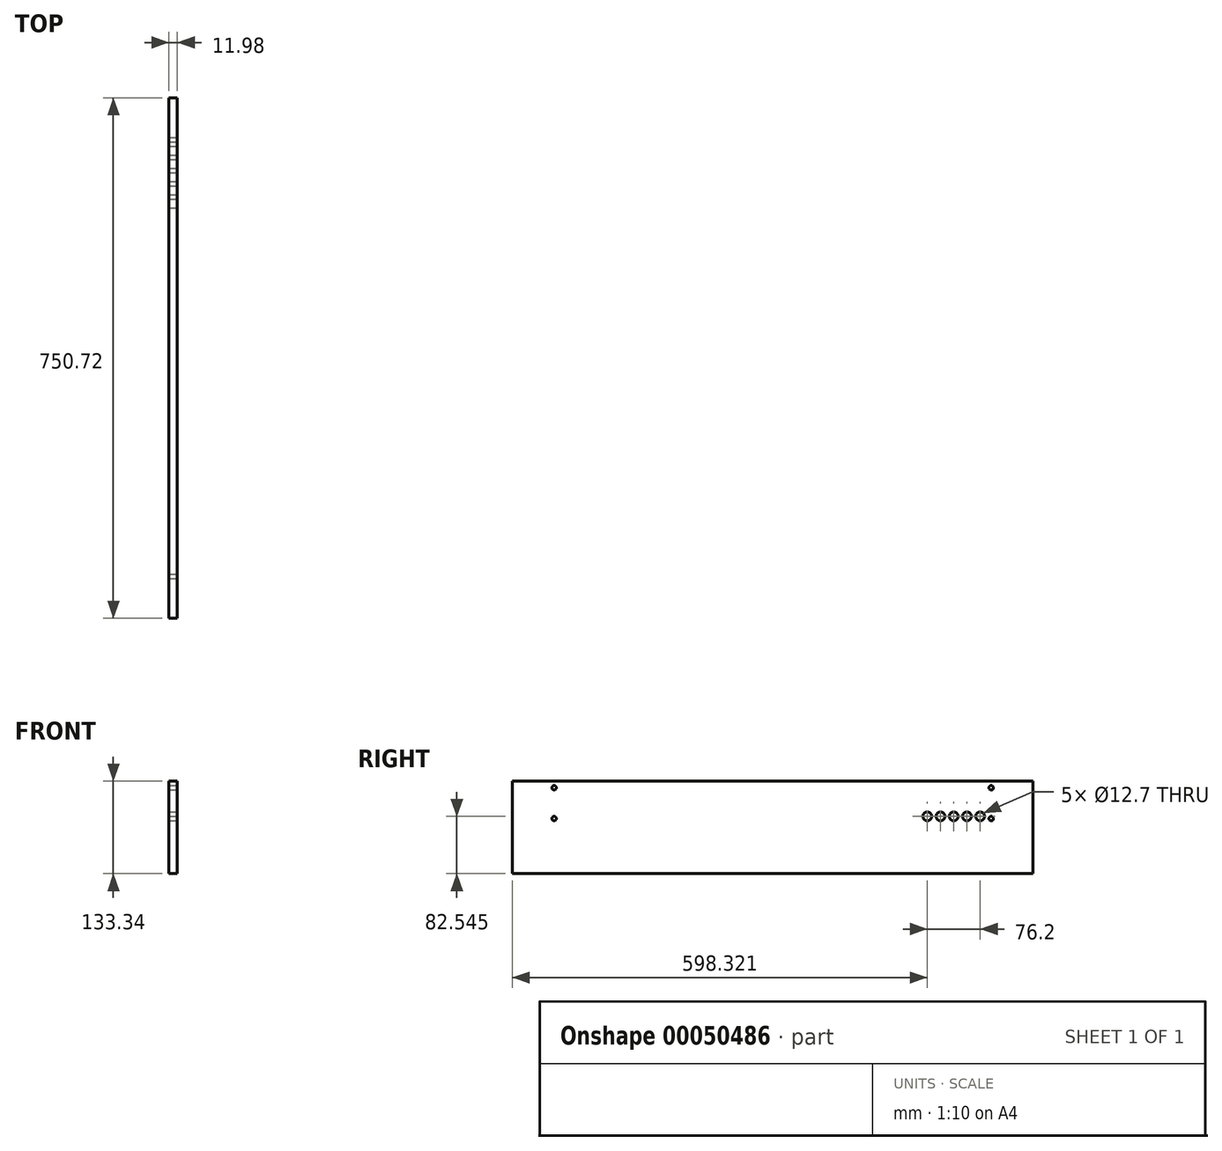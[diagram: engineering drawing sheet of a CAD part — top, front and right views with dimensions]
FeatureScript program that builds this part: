
annotation { "Feature Type Name" : "Feature", "Feature Type Description" : "" }
export const myFeature = defineFeature(function(context is Context, id is Id, definition is map)
    precondition{}
    {
        {
            var Q0;
            Q0=qCreatedBy(makeId("Right.planeOp"),FACE);
            var sketch = newSketch(context, id + "F0", { "sketchPlane" : qUnion([Q0])});
            skLineSegment(sketch, "E0.rect.bottom", {"start": v(375.36, -66.67) * mm, "end": v(-375.36, -66.67) * mm});
            skLineSegment(sketch, "E0.rect.top", {"start": v(375.36, 66.68) * mm, "end": v(-375.36, 66.67) * mm});
            skLineSegment(sketch, "E0.rect.left", {"start": v(375.36, -66.67) * mm, "end": v(375.36, 66.68) * mm});
            skLineSegment(sketch, "E0.rect.right", {"start": v(-375.36, -66.67) * mm, "end": v(-375.36, 66.68) * mm});
            skPoint(sketch, "E0.rect.middle", {"position": v(0, 0) * mm});
            skSolve(sketch);
        }
        {
            var Q0;
            Q0 = qSketchRegion(id + "F0", true);
            extrude(context, id + "F1", {"entities" : qUnion([Q0]), "endBound" : BoundingType.SYMMETRIC, "depth" : 12 * mm});
        }
        {
            var Q0;
            Q0=makeQuery(id+"F1.opExtrude","CAP_FACE",FACE,{"disambiguationData":[OSD([sQuery(id+"F0.wireOp",EDGE,"E0.rect.bottom"),sQuery(id+"F0.wireOp",EDGE,"E0.rect.top"),sQuery(id+"F0.wireOp",EDGE,"E0.rect.left"),sQuery(id+"F0.wireOp",EDGE,"E0.rect.right")])],"isStart":false});
            var sketch = newSketch(context, id + "F2", { "sketchPlane" : qUnion([Q0])});
            skLineSegment(sketch, "E1", {"start": v(-375.36, 15.88) * mm, "end": v(375.36, 15.88) * mm, "construction": true});
            skCircle(sketch, "E2", {"center": v(222.96, 15.88) * mm, "radius": 6.35 * mm});
            skCircle(sketch, "E3", {"center": v(242.01, 15.88) * mm, "radius": 6.35 * mm});
            skCircle(sketch, "E4", {"center": v(261.06, 15.88) * mm, "radius": 6.35 * mm});
            skCircle(sketch, "E5", {"center": v(280.11, 15.88) * mm, "radius": 6.35 * mm});
            skCircle(sketch, "E6", {"center": v(299.16, 15.88) * mm, "radius": 6.35 * mm});
            skSolve(sketch);
        }
        {
            var Q0;
            Q0 = qSketchRegion(id + "F2", true);
            extrude(context, id + "F3", {"entities" : qUnion([Q0]), "operationType" : NewBodyOperationType.REMOVE, "endBound" : BoundingType.UP_TO_NEXT, "oppositeDirection" : true, "depth" : 25.4 * mm});
        }
        {
            var Q0;
            Q0=makeQuery(id+"F1.opExtrude","CAP_FACE",FACE,{"disambiguationData":[OSD([sQuery(id+"F0.wireOp",EDGE,"E0.rect.bottom"),sQuery(id+"F0.wireOp",EDGE,"E0.rect.top"),sQuery(id+"F0.wireOp",EDGE,"E0.rect.left"),sQuery(id+"F0.wireOp",EDGE,"E0.rect.right")])],"isStart":false});
            var sketch = newSketch(context, id + "F4", { "sketchPlane" : qUnion([Q0])});
            skLineSegment(sketch, "E7.bottom", {"start": v(-315.04, 57.15) * mm, "end": v(315.04, 57.15) * mm, "construction": true});
            skLineSegment(sketch, "E7.top", {"start": v(-315.04, 12.7) * mm, "end": v(315.04, 12.7) * mm, "construction": true});
            skLineSegment(sketch, "E7.left", {"start": v(-315.04, 57.15) * mm, "end": v(-315.04, 12.7) * mm, "construction": true});
            skLineSegment(sketch, "E7.right", {"start": v(315.04, 57.15) * mm, "end": v(315.04, 12.7) * mm, "construction": true});
            skCircle(sketch, "E8", {"center": v(-315.04, 57.15) * mm, "radius": 3.18 * mm});
            skCircle(sketch, "E9", {"center": v(-315.04, 12.7) * mm, "radius": 3.18 * mm});
            skCircle(sketch, "E10", {"center": v(315.04, 12.7) * mm, "radius": 3.18 * mm});
            skCircle(sketch, "E11", {"center": v(315.04, 57.15) * mm, "radius": 3.18 * mm});
            skSolve(sketch);
        }
        {
            var Q0;
            Q0 = qSketchRegion(id + "F4", true);
            extrude(context, id + "F5", {"entities" : qUnion([Q0]), "operationType" : NewBodyOperationType.REMOVE, "endBound" : BoundingType.UP_TO_NEXT, "oppositeDirection" : true, "depth" : 25.4 * mm});
        }
    });
